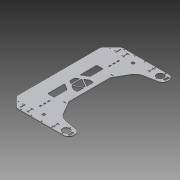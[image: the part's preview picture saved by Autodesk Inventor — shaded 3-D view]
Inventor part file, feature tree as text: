
AUTODESK INVENTOR PART (.ipt)
format: ipt  version: 2015 (Build 190159000, 159)  size: 520,192 bytes
history: native  units: mm
features: extrude x4, sketch x4, fillet x3, other x3
ambient origin geometry x8: Origin, YZ Plane, XZ Plane, XY Plane, X Axis, Y Axis, Z Axis, Center Point
bodies: Body1 (feature_tree)
feature tree (14):
  extrude  "Extrusion22"  Depth=5.0mm
  extrude  "Extrusion23"  Depth=40.0mm
  extrude  "Extrusion24"  Depth=20.0mm
  fillet  "Fillet15"  Radius=25.923375mm
  fillet  "Fillet16"  Radius=12.0mm
  extrude  "Extrusion25"  Depth=3.0mm TaperAngle=0.0deg
  fillet  "Fillet18"  Radius=3.0mm
  other  "Bend Part35"
  other  "Bend Part36"
  other  "Profile"
  sketch  "Sketch41"  dims[d19=5.0mm d127=97.0mm d151=5.0mm d163=5.0mm]
  sketch  "Sketch42"  dims[d222=5.0mm d248=40.0mm]
  sketch  "Sketch43"  dims[d294=25.0mm]
  sketch  "Sketch44"  dims[d324=5.0mm d326=25.0mm d329=25.0mm d344=6.0mm d358=6.0mm d404=5.0mm d406=45.0mm d445=20.0mm d446=30.0mm d448=45.0deg d460=5.606189mm d463=30.0deg d467=42.0mm d468=36.0mm d469=150.0deg d483=12.0mm d486=42.0mm d487=150.0deg d488=36.0mm d489=150.0deg d528=20.0mm d530=65.0mm d567=25.923375mm d595=12.0mm d615=3.0mm d616=0.0mm d624=3.0mm d628=10.0mm d629=0.0mm d630=20.0mm d631=53.0mm d633=85.0mm d635=10.0mm d636=0.0mm d637=5.0mm d638=2.0mm d639=1.0mm d640=90.0deg d641=1.0mm d642=90.0deg d646=100.0mm d649=5.0mm d651=50.0mm d653=50.0mm d654=10.0mm d656=10.0mm d658=239.0mm d659=32.0mm d660=5.0mm d665=150.0deg d666=50.0mm d668=220.0mm d673=13.0mm d675=3.0mm d677=1.0mm d678=12.0mm d679=43.0mm d680=6.0mm d681=10.0mm d682=47.0mm d684=30.0mm d686=20.0mm d687=10.0mm d689=10.0mm d691=25.0mm d695=20.0mm d699=3.0mm d703=3.0mm d708=5.0mm d710=150.0mm d711=58.284271mm d713=5.0mm d714=33.0mm d716=45.0deg d717=22.847192mm d720=54.461397mm d722=155.0mm d723=32.0mm d724=240.0mm d725=5.0mm d726=2.0mm d727=2.0mm d728=13.0mm d729=10.0mm d730=0.0mm d731=20.0mm d732=24.0mm d733=4.0mm d734=0.5mm d735=22.0mm d736=10.0mm d737=0.5mm d738=25.0mm d740=60.0mm d742=5.0mm d743=10.0mm d745=1.0mm d747=50.0mm d749=5.0mm d750=10.0mm d752=10.0mm d754=35.0mm d755=20.5mm d757=27.0mm d758=3.0mm d759=20.0mm d760=80.0mm d762=60.0deg d767=5.0mm d768=5.0mm d769=25.923375mm d774=5.0mm d775=16.0mm d777=65.0mm d779=16.0mm d780=21.354042mm d782=2.0mm d794=4.0mm d795=4.0mm d796=25.0mm d798=3.0mm d799=25.5mm d800=30.5mm]
